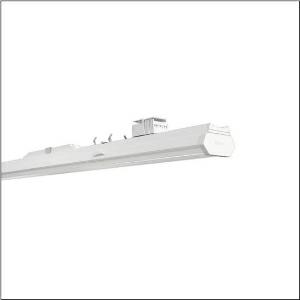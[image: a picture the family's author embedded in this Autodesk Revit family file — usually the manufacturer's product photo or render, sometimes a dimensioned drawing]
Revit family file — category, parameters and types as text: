
# Revit family: licross_r__11_protected_mo_51tp12cn685g_00be
name_source: partatom
category: Lighting Fixtures
units: mm (PartAtom-declared; Revit-internal decimal feet)

## family parameters
Cut with Voids When Loaded = No
Host = Face
Light Source = No
Part Type = Normal
Room Calculation Point = No
Round Connector Dimension = Use Diameter
Shared = No

## types (1)
- --- (1 x LED, 8840 lm, 49.4 W, 6500K)
    Apparent Load = 49 VA
    CIE Flux Codes = 73 92 98 99 100
    Color Rendering = 80
    Color Temperature = 6500K
    Default Elevation = 1800 mm
    Description = Licross® 11 Protected MO, luminaire insert, of sheet steel, galvanised, coil coated, white, length: 1.500mm, width: 90mm, height: 101mm, LED rated luminous flux: 8.840lm, light colour: 865, control gear: ON/OFF Multilumen, CLOi, with plug, 3-pole, with phase selection, mains connection: 220..240V, AC, 50/60Hz, start of lifetime: 49W, end of service life: 55W, internal wiring halogen-free, primary light control with lens, of plastic, primary optical cover: cover, of PMMA, light emission: direct distribution, primary light characteristic: symmetric, protection rating (complete): IP64, insulation class (complete): insulation class I (protective earthing), certification: CE, ENEC, VDE, UKCA, protection symbol: D if used in an environment with conductive dust loads with corresponding accessories, impact resistance: IK06, permissible ambient temperature for indoor applications: -35..+40°C, corresponds to IFS (International Featured Standards) requirements for safety and quality in the food industry, reducing of maximum allowable ambient temperature of 5°C with ceiling mounting, LABS conformity tested according to VDMA 24364:2018-05, packaging unit: 1 piece
    Height = 92 mm
    Lamp = 1 x LED
    Lamp Light Flux = 8840 lm
    Lamp Power = 49.4 W
    Lamp count = 1
    Length = 1500 mm
    Luminous efficacy = 179 lm/W
    Manufacturer = Siteco
    ModVariant = No
    Model = 51TP12CN685G
    Mounting Place = Ceiling
    Mounting Type = Pendant
    Number of Poles = 1
    OnlyDefault = Yes
    Power Factor = 1
    Product Name = Licross® 11 Protected MO
    Product group = luminaire insert | ceiling pendant
    ProductGroupID = 902
    Protection Class = Protection class I
    Protection Degree = IP 64
    RLX_Detail_Level = 1
    RLX_Emergency_Light_Flux = 0 lm
    RLX_Emergency_Type = 0
    RLX_Emergency_Type_DB = No
    RlxData = <blob elided: 22085 chars, md5=f2cce436>
    Socket = socket
    Standby Power = 0 W
    System Light Flux = 8840 lm
    System Power = 49 W
    Type Comments = factory setting: luminous flux: 100 % | (A | C | E) | 113 mA
    Type Image = l_1256148.jpg
    URL = http://relux.com
    VarID = @adj_030365
    Voltage = 0 V
    Weight = 0.00 kg
    Width = 88 mm

## geometry (parser evidence)
native form markers: Blend x4, Sweep x10
no freeform markers — native parametric forms only
